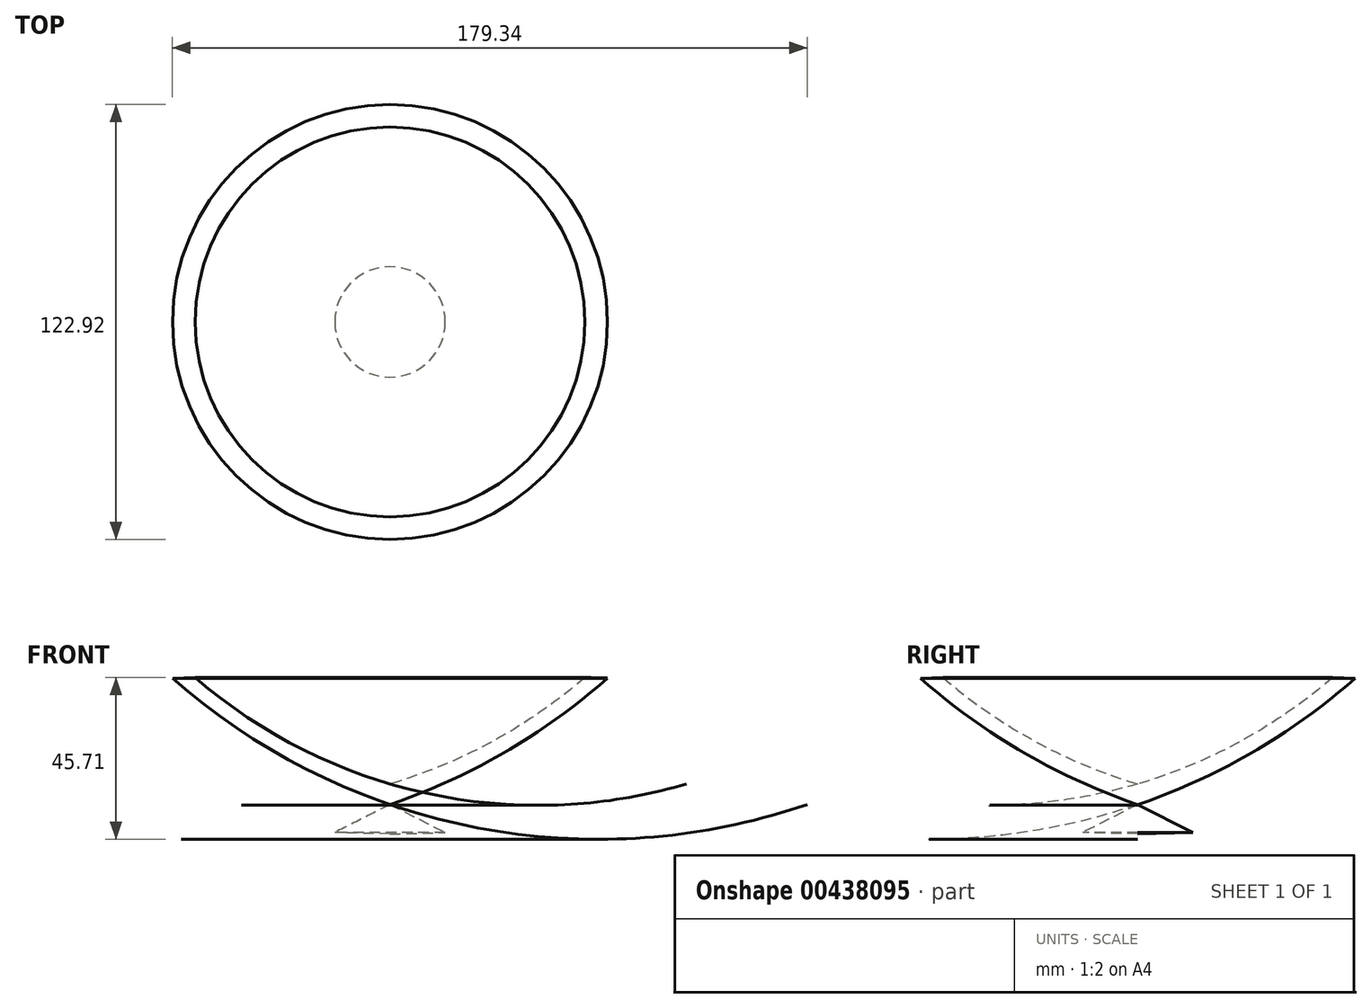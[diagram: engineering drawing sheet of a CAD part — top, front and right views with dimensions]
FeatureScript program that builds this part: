
annotation { "Feature Type Name" : "Feature", "Feature Type Description" : "" }
export const myFeature = defineFeature(function(context is Context, id is Id, definition is map)
    precondition{}
    {
        {
            var Q0;
            Q0=qCreatedBy(makeId("Front.planeOp"),FACE);
            var sketch = newSketch(context, id + "F0", { "sketchPlane" : qUnion([Q0])});
            skLineSegment(sketch, "E0", {"start": v(0, 51.69) * mm, "end": v(0, -47.36) * mm, "construction": true});
            skArc(sketch, "E1", {"start": v(-61.46, 9.96) * mm, "mid": v(-32.49, -10.92) * mm, "end": v(0, -25.75) * mm});
            skArc(sketch, "E2", {"start": v(-55.07, 10.15) * mm, "mid": v(-29.14, -7.83) * mm, "end": v(0, -19.92) * mm});
            skLineSegment(sketch, "E3", {"start": v(-55.07, 10.15) * mm, "end": v(-61.46, 9.96) * mm});
            skLineSegment(sketch, "E4", {"start": v(0, -25.75) * mm, "end": v(0, -19.92) * mm});
            skLineSegment(sketch, "E5", {"start": v(0, -25.75) * mm, "end": v(-15.6, -33.64) * mm});
            skLineSegment(sketch, "E6", {"start": v(-15.6, -33.64) * mm, "end": v(0, -34.06) * mm});
            skLineSegment(sketch, "E7", {"start": v(0, -34.06) * mm, "end": v(0, -25.75) * mm});
            skSolve(sketch);
        }
        {
            var Q0;
            Q0=makeQuery(id+"F0.imprint","IMPRINT",FACE,{"disambiguationData":[TD([[makeQuery(id+"F0.imprint","IMPRINT",EDGE,{"derivedFrom":sQuery(id+"F0.wireOp",EDGE,"E1")}),1.0]])]});
            var Q1;
            Q1=makeQuery(id+"F0.imprint","IMPRINT",FACE,{"disambiguationData":[TD([[makeQuery(id+"F0.imprint","IMPRINT",EDGE,{"derivedFrom":sQuery(id+"F0.wireOp",EDGE,"E5")}),1.0]])]});
            var Q2;
            Q2=sQuery(id+"F0.wireOp",EDGE,"E0");
            revolve(context, id + "F1", {"entities" : qUnion([Q0, Q1]), "axis" : qUnion([Q2]), "revolveType" : RevolveType.FULL});
        }
    });
